# Revit family: 351_e59da2b0014d41a9b1ae3992a0905d
name_source: partatom
category: Plumbing Fixtures
units: mm (PartAtom-declared; Revit-internal decimal feet)

## family parameters
Always vertical = Yes
Cut with Voids When Loaded = No
Part Type = Normal
Room Calculation Point = No
Round Connector Dimension = Use Diameter
Shared = No
Work Plane-Based = No

## types (1)
- 5611183 IDO GLOW
    CAT0 = Yes
    CLBTZ = 0 mm  [stored 0 ft]
    CL_Location_5000 = 5000 mm  [stored 16.4042 ft]
    D = 50 mm
    Description = Washbasin IDO Glow 500x360, square, no overflow
    Manufacturer = IDO
    OH = No
    QmdConnectorList = 601;D
    R = 27 mm  [stored 0.0885827 ft]
    TH = Yes
    URL = http://www.ido.fi
    XRefLineVPlnId = 7453
    YRefLineVPlnId = 7456
    magiPartTypeId = 351
    magiProductCode = 5611183 IDO GLOW
    magiProductFamilyId = e59da2b0014d41a9b1ae3992a0905d
    magiProductId = e59da2b0014d41a9b1ae3992a0905d

note: [stored X ft] marks values corroborated as IEEE doubles in the binary element streams (Revit-internal decimal feet)

## geometry (parser evidence)
native form markers: Sweep x2
no freeform markers — native parametric forms only
